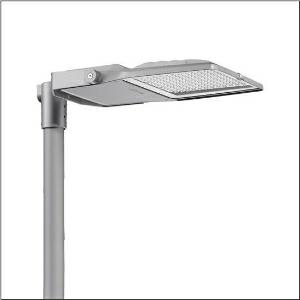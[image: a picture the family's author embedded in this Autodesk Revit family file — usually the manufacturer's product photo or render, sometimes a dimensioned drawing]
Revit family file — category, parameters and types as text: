
# Revit family: floodlight_fl_21_midi___pl64_5xa7786e4e3a_f47e
name_source: partatom
category: Lighting Fixtures
units: mm (PartAtom-declared; Revit-internal decimal feet)

## family parameters
Cut with Voids When Loaded = No
Host = Face
Light Source = No
Part Type = Normal
Room Calculation Point = No
Round Connector Dimension = Use Diameter
Shared = No

## types (1)
- --- (1 x LED, 27140 lm, 212.4 W, 4000K)
    Apparent Load = 212 VA
    CIE Flux Codes = 28 80 98 100 100
    Color Rendering = 70
    Color Temperature = 4000K
    Default Elevation = 1800 mm
    Description = Floodlight FL 21 midi, floodlight, primary light control with lens, of PMMA, primary optical cover: protective disc, of toughened safety glass, transparent, light distribution: PL64, light emission: direct distribution, installation type: surface-mounted, LED, High Power LED, rated luminous flux: 27.140lm, luminous efficacy: 128lm/W, light colour: 740, colour temperature: 4000K, control gear: Smart Interface (Zhaga)D4i, control: overheat protection, constant luminous flux control, time-dependent luminous flux control, flexible luminous flux parameterisation, pre-setting: logarithmic dimming characteristic, with terminal, 6-pole, mains connection: 220..240V, AC, 50/60Hz, start of lifetime: 212W, end of service life: 231W, reduction: 95W, mast bracket, of diecast aluminium, powder-coated, SITECO metallic grey (DB 702S), corrosivity category C5 mid according to DIN EN ISO 12944, suitable for swimming pools, chlorine-resistant, sealing non-destructively replaceable, mast bracket, of steel, galvanised, powder-coated, SITECO metallic grey (DB 702S), Smart Interface below and above, protection rating (complete): IP66, insulation class (complete): insulation class II (safety insulation), certification: CE, ENEC, VDE, protection symbol: D, impact resistance: IK08, permissible operating ambient temperature: -40..+40°C, permissible operating ambient temperature for outdoor applications: -40..+50°C, standard: DIN EN 12944, LABS conformity tested according to VDMA 24364:2018-05, packaging unit: 1 piece

Light Distribution: PL64
    Height = 76 mm
    Lamp = 1 x LED
    Lamp Light Flux = 27140 lm
    Lamp Power = 212.4 W
    Lamp count = 1
    Length = 657 mm
    Luminous efficacy = 128 lm/W
    Manufacturer = Siteco
    ModVariant = No
    Model = 5XA7786E4E3A
    Number of Poles = 1
    OnlyDefault = Yes
    Power Factor = 1
    Product Name = Floodlight FL 21 midi | PL64
    Product group = floodlight | pylon annexe
    ProductGroupID = 6201
    Protection Class = Protection class II
    Protection Degree = IP 66
    RLX_Detail_Level = 1
    RLX_Emergency_Light_Flux = 0 lm
    RLX_Emergency_Type = 0
    RLX_Emergency_Type_DB = No
    RlxData = <blob elided: 104697 chars, md5=201d1adf>
    Socket = socket
    Standby Power = 0 W
    System Light Flux = 27140 lm
    System Power = 212 W
    Type Comments = factory setting: luminous flux: 100 % | dim-lin: 254 | 710 mA
    Type Image = l_1007123.jpg
    URL = http://relux.com
    VarID = @adj_093301
    Voltage = 0 V
    Weight = 0.00 kg
    Width = 442 mm

## geometry (parser evidence)
native form markers: Blend x4, Sweep x11
no freeform markers — native parametric forms only
